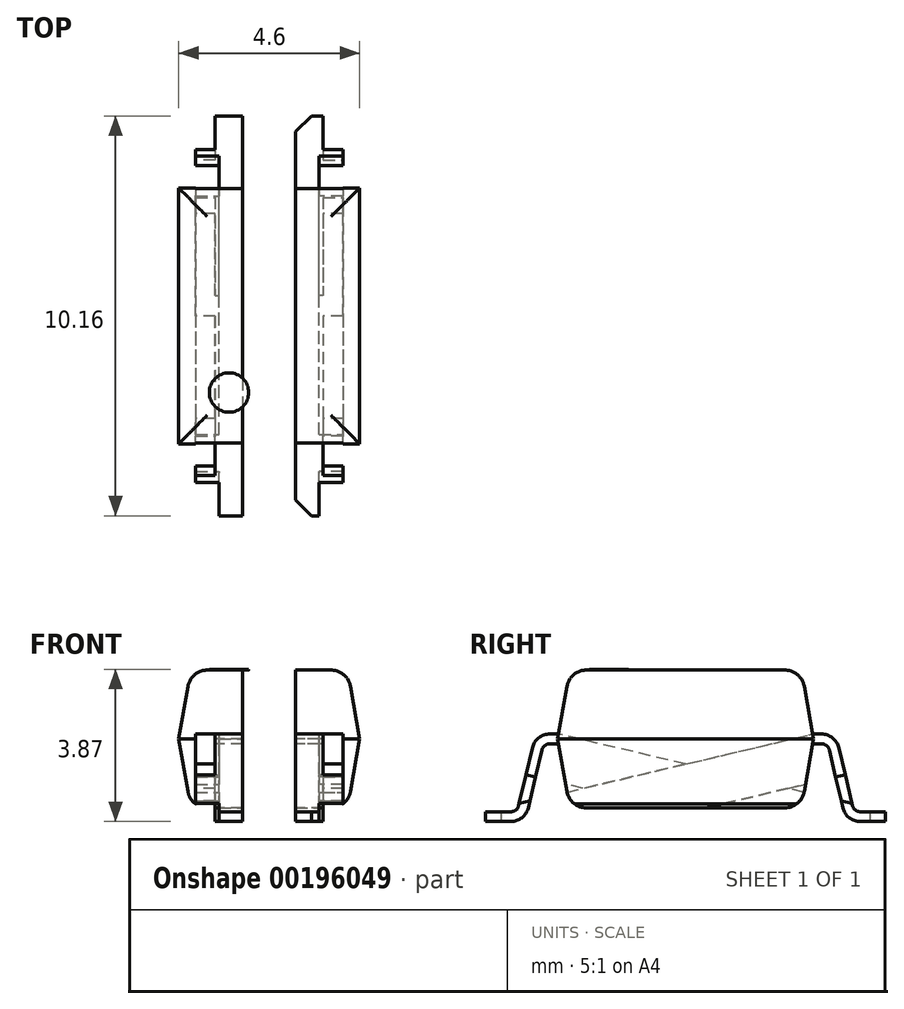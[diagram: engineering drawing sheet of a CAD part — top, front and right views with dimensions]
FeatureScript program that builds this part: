
annotation { "Feature Type Name" : "Feature", "Feature Type Description" : "" }
export const myFeature = defineFeature(function(context is Context, id is Id, definition is map)
    precondition{}
    {
        {
            var Q0;
            Q0=qCreatedBy(makeId("Top.planeOp"),FACE);
            var sketch = newSketch(context, id + "F0", { "sketchPlane" : qUnion([Q0])});
            skLineSegment(sketch, "E0.bottom", {"start": v(2.3, -3.25) * mm, "end": v(-2.3, -3.25) * mm});
            skLineSegment(sketch, "E0.top", {"start": v(2.3, 3.25) * mm, "end": v(-2.3, 3.25) * mm});
            skLineSegment(sketch, "E0.left", {"start": v(2.3, -3.25) * mm, "end": v(2.3, 3.25) * mm});
            skLineSegment(sketch, "E0.right", {"start": v(-2.3, -3.25) * mm, "end": v(-2.3, 3.25) * mm});
            skPoint(sketch, "E0.middle", {"position": v(0, 0) * mm});
            skSolve(sketch);
        }
        {
            var Q0;
            Q0 = qSketchRegion(id + "F0", true);
            extrude(context, id + "F1", {"entities" : qUnion([Q0]), "depth" : 1.75 * mm, "hasDraft" : true, "draftAngle" : 10 * degree, "draftPullDirection" : true});
        }
        {
            var Q0;
            Q0 = qSketchRegion(id + "F0", true);
            extrude(context, id + "F2", {"entities" : qUnion([Q0]), "operationType" : NewBodyOperationType.ADD, "oppositeDirection" : true, "depth" : 1.75 * mm, "hasDraft" : true, "draftAngle" : 10 * degree, "draftPullDirection" : true});
        }
        {
            var Q0;
            Q0=makeQuery(id+"F1.opExtrude","CAP_FACE",FACE,{"disambiguationData":[OSD([sQuery(id+"F0.wireOp",EDGE,"E0.bottom"),sQuery(id+"F0.wireOp",EDGE,"E0.top"),sQuery(id+"F0.wireOp",EDGE,"E0.left"),sQuery(id+"F0.wireOp",EDGE,"E0.right")])],"isStart":false});
            var Q1;
            Q1=makeQuery(id+"F2.opExtrude","CAP_FACE",FACE,{"disambiguationData":[OSD([sQuery(id+"F0.wireOp",EDGE,"E0.bottom"),sQuery(id+"F0.wireOp",EDGE,"E0.top"),sQuery(id+"F0.wireOp",EDGE,"E0.left"),sQuery(id+"F0.wireOp",EDGE,"E0.right")])],"isStart":false});
            fillet(context, id + "F3", {"entities" : qUnion([Q0, Q1]), "radius" : 0.5 * mm, "tangentPropagation" : true, "allowEdgeOverflow" : false});
        }
        {
            var Q0;
            Q0=qCreatedBy(makeId("Right.planeOp"),FACE);
            var sketch = newSketch(context, id + "F4", { "sketchPlane" : qUnion([Q0])});
            skLineSegment(sketch, "E1", {"start": v(3.81, 0.13) * mm, "end": v(4.28, -1.85) * mm});
            skLineSegment(sketch, "E2", {"start": v(4.28, -1.85) * mm, "end": v(5.08, -1.85) * mm});
            skLineSegment(sketch, "E3.0", {"start": v(4.08, -2.1) * mm, "end": v(5.08, -2.1) * mm});
            skLineSegment(sketch, "E4", {"start": v(5.08, -1.85) * mm, "end": v(5.08, -2.1) * mm});
            skLineSegment(sketch, "E5", {"start": v(0, 0) * mm, "end": v(0, -1.75) * mm, "construction": true});
            skLineSegment(sketch, "E6.MirrorCS", {"start": v(3.23, 0.13) * mm, "end": v(3.25, 0) * mm});
            skLineSegment(sketch, "E7", {"start": v(4.28, -1.85) * mm, "end": v(4.03, -1.9) * mm, "construction": true});
            skLineSegment(sketch, "E8", {"start": v(4.28, -1.85) * mm, "end": v(4.28, -2.1) * mm, "construction": true});
            skLineSegment(sketch, "E9", {"start": v(3.23, 0.13) * mm, "end": v(3.8, 0.13) * mm});
            skLineSegment(sketch, "E10", {"start": v(3.25, 0) * mm, "end": v(3.23, -0.12) * mm});
            skLineSegment(sketch, "E11", {"start": v(3.23, -0.12) * mm, "end": v(3.61, -0.12) * mm});
            skLineSegment(sketch, "E12", {"start": v(3.61, -0.12) * mm, "end": v(4.08, -2.1) * mm});
            skLineSegment(sketch, "E13", {"start": v(3.61, -0.12) * mm, "end": v(3.61, 0.13) * mm, "construction": true});
            skLineSegment(sketch, "E14.MirrorCS", {"start": v(-3.23, 0.13) * mm, "end": v(-3.25, 0) * mm});
            skLineSegment(sketch, "E15.MirrorCS", {"start": v(-3.25, 0) * mm, "end": v(-3.23, -0.12) * mm});
            skLineSegment(sketch, "E16.MirrorCS", {"start": v(-4.28, -1.85) * mm, "end": v(-4.03, -1.9) * mm, "construction": true});
            skLineSegment(sketch, "E17.MirrorCS", {"start": v(-5.08, -1.85) * mm, "end": v(-5.08, -2.1) * mm});
            skLineSegment(sketch, "E18.MirrorCS", {"start": v(-3.23, -0.12) * mm, "end": v(-3.61, -0.12) * mm});
            skLineSegment(sketch, "E19.MirrorCS", {"start": v(-3.61, -0.12) * mm, "end": v(-4.08, -2.1) * mm});
            skLineSegment(sketch, "E20.MirrorCS", {"start": v(-4.28, -1.85) * mm, "end": v(-4.28, -2.1) * mm, "construction": true});
            skLineSegment(sketch, "E21.MirrorCS", {"start": v(-3.61, -0.12) * mm, "end": v(-3.61, 0.13) * mm, "construction": true});
            skLineSegment(sketch, "E22.MirrorCS", {"start": v(-3.8, 0.12) * mm, "end": v(-4.28, -1.85) * mm});
            skLineSegment(sketch, "E23.MirrorCS", {"start": v(-4.28, -1.85) * mm, "end": v(-5.08, -1.85) * mm});
            skLineSegment(sketch, "E24.MirrorCS", {"start": v(-3.23, 0.13) * mm, "end": v(-3.8, 0.13) * mm});
            skLineSegment(sketch, "E25.MirrorCS", {"start": v(-4.08, -2.1) * mm, "end": v(-5.08, -2.1) * mm});
            skLineSegment(sketch, "E26", {"start": v(3.25, 0) * mm, "end": v(3.61, 0) * mm, "construction": true});
            skSolve(sketch);
        }
        {
            var Q0;
            Q0 = qSketchRegion(id + "F4", true);
            extrude(context, id + "F5", {"entities" : qUnion([Q0]), "endBound" : BoundingType.SYMMETRIC, "depth" : 3.74 * mm});
        }
        {
            var Q0;
            Q0=qCreatedBy(makeId("Top.planeOp"),FACE);
            var sketch = newSketch(context, id + "F6", { "sketchPlane" : qUnion([Q0])});
            skLineSegment(sketch, "E27.bottom", {"start": v(-0.67, 5.08) * mm, "end": v(0.67, 5.08) * mm});
            skLineSegment(sketch, "E27.top", {"start": v(-0.67, -5.08) * mm, "end": v(0.67, -5.08) * mm});
            skLineSegment(sketch, "E27.left", {"start": v(-0.67, 5.08) * mm, "end": v(-0.67, -5.08) * mm});
            skLineSegment(sketch, "E27.right", {"start": v(0.67, 5.08) * mm, "end": v(0.67, -5.08) * mm});
            skPoint(sketch, "E27.middle", {"position": v(0, 0) * mm});
            skSolve(sketch);
        }
        {
            var Q0;
            Q0 = qSketchRegion(id + "F6", true);
            extrude(context, id + "F7", {"entities" : qUnion([Q0]), "operationType" : NewBodyOperationType.REMOVE, "endBound" : BoundingType.THROUGH_ALL, "oppositeDirection" : true, "depth" : 25 * mm, "hasSecondDirection" : true, "secondDirectionBound" : SecondDirectionBoundingType.THROUGH_ALL, "secondDirectionOppositeDirection" : false, "secondDirectionDepth" : 25 * mm});
        }
        {
            var Q0;
            Q0=makeQuery(id+"F7.boolean.opBoolean","COPY",EDGE,{"derivedFrom":makeQuery(id+"F7.opExtrude","SWEPT_EDGE",EDGE,{"disambiguationData":[OSD([sQuery(id+"F6.wireOp",EDGE,"E27.top"),sQuery(id+"F6.wireOp",EDGE,"E27.left")])]})});
            var Q1;
            Q1=makeQuery(id+"F5.opExtrude","CAP_EDGE",EDGE,{"disambiguationData":[OSD([sQuery(id+"F4.wireOp",EDGE,"E17.MirrorCS")])],"isStart":true});
            var Q2;
            Q2=makeQuery(id+"F7.boolean.opBoolean","COPY",EDGE,{"derivedFrom":makeQuery(id+"F7.opExtrude","SWEPT_EDGE",EDGE,{"disambiguationData":[OSD([sQuery(id+"F6.wireOp",EDGE,"E27.top"),sQuery(id+"F6.wireOp",EDGE,"E27.right")])]})});
            var Q3;
            Q3=makeQuery(id+"F5.opExtrude","CAP_EDGE",EDGE,{"disambiguationData":[OSD([sQuery(id+"F4.wireOp",EDGE,"E17.MirrorCS")])],"isStart":false});
            var Q4;
            Q4=makeQuery(id+"F7.boolean.opBoolean","COPY",EDGE,{"derivedFrom":makeQuery(id+"F7.opExtrude","SWEPT_EDGE",EDGE,{"disambiguationData":[OSD([sQuery(id+"F6.wireOp",EDGE,"E27.bottom"),sQuery(id+"F6.wireOp",EDGE,"E27.right")])]})});
            var Q5;
            Q5=makeQuery(id+"F7.boolean.opBoolean","COPY",EDGE,{"derivedFrom":makeQuery(id+"F7.opExtrude","SWEPT_EDGE",EDGE,{"disambiguationData":[OSD([sQuery(id+"F6.wireOp",EDGE,"E27.bottom"),sQuery(id+"F6.wireOp",EDGE,"E27.left")])]})});
            var Q6;
            Q6=makeQuery(id+"F5.opExtrude","CAP_EDGE",EDGE,{"disambiguationData":[OSD([sQuery(id+"F4.wireOp",EDGE,"E4")])],"isStart":true});
            var Q7;
            Q7=makeQuery(id+"F5.opExtrude","CAP_EDGE",EDGE,{"disambiguationData":[OSD([sQuery(id+"F4.wireOp",EDGE,"E4")])],"isStart":false});
            chamfer(context, id + "F8", {"entities" : qUnion([Q0, Q1, Q2, Q3, Q4, Q5, Q6, Q7]), "width" : 0.4 * mm, "tangentPropagation" : true});
        }
        {
            var Q0;
            {var subQ2=sQuery(id+"F4.wireOp",EDGE,"E22.MirrorCS");Q0=makeQuery(id+"F7.boolean.opBoolean","SPLIT",FACE,{"disambiguationData":[TD([makeQuery(id+"F7.opExtrude","SWEPT_FACE",FACE,{"disambiguationData":[OSD([sQuery(id+"F6.wireOp",EDGE,"E27.left")])]})])],"derivedFrom":makeQuery(id+"F5.opExtrude","SWEPT_FACE",FACE,{"disambiguationData":[OSD([subQ2])]})});}
            var sketch = newSketch(context, id + "F9", { "sketchPlane" : qUnion([Q0])});
            skLineSegment(sketch, "E28.bottom", {"start": v(-1.87, -0.62) * mm, "end": v(-1.37, -0.62) * mm});
            skLineSegment(sketch, "E28.top", {"start": v(-1.87, -1.82) * mm, "end": v(-1.37, -1.82) * mm});
            skLineSegment(sketch, "E28.left", {"start": v(-1.87, -0.62) * mm, "end": v(-1.87, -1.82) * mm});
            skLineSegment(sketch, "E28.right", {"start": v(-1.37, -0.62) * mm, "end": v(-1.37, -1.82) * mm});
            skLineSegment(sketch, "E29", {"start": v(0, 0) * mm, "end": v(0, -3.26) * mm, "construction": true});
            skLineSegment(sketch, "E30.MirrorCS", {"start": v(1.87, -1.82) * mm, "end": v(1.37, -1.82) * mm});
            skLineSegment(sketch, "E31.MirrorCS", {"start": v(1.87, -0.62) * mm, "end": v(1.37, -0.62) * mm});
            skLineSegment(sketch, "E32.MirrorCS", {"start": v(1.37, -0.62) * mm, "end": v(1.37, -1.82) * mm});
            skLineSegment(sketch, "E33.MirrorCS", {"start": v(1.87, -0.62) * mm, "end": v(1.87, -1.82) * mm});
            skSolve(sketch);
        }
        {
            var Q0;
            Q0 = qSketchRegion(id + "F9", true);
            extrude(context, id + "F10", {"entities" : qUnion([Q0]), "operationType" : NewBodyOperationType.REMOVE, "oppositeDirection" : true, "depth" : 25 * mm});
        }
        {
            var Q0;
            {var subQ2=sQuery(id+"F4.wireOp",EDGE,"E1");Q0=makeQuery(id+"F7.boolean.opBoolean","SPLIT",FACE,{"disambiguationData":[TD([makeQuery(id+"F7.opExtrude","SWEPT_FACE",FACE,{"disambiguationData":[OSD([sQuery(id+"F6.wireOp",EDGE,"E27.right")])]})])],"derivedFrom":makeQuery(id+"F5.opExtrude","SWEPT_FACE",FACE,{"disambiguationData":[OSD([subQ2])]})});}
            var sketch = newSketch(context, id + "F11", { "sketchPlane" : qUnion([Q0])});
            skLineSegment(sketch, "E34.bottom", {"start": v(-1.87, -0.62) * mm, "end": v(-1.27, -0.62) * mm});
            skLineSegment(sketch, "E34.top", {"start": v(-1.87, -1.82) * mm, "end": v(-1.27, -1.82) * mm});
            skLineSegment(sketch, "E34.left", {"start": v(-1.87, -0.62) * mm, "end": v(-1.87, -1.82) * mm});
            skLineSegment(sketch, "E34.right", {"start": v(-1.27, -0.62) * mm, "end": v(-1.27, -1.82) * mm});
            skLineSegment(sketch, "E35", {"start": v(0, 0) * mm, "end": v(0, -3.04) * mm, "construction": true});
            skLineSegment(sketch, "E36.MirrorCS", {"start": v(1.87, -0.62) * mm, "end": v(1.27, -0.62) * mm});
            skLineSegment(sketch, "E37.MirrorCS", {"start": v(1.87, -1.82) * mm, "end": v(1.27, -1.82) * mm});
            skLineSegment(sketch, "E38.MirrorCS", {"start": v(1.87, -0.62) * mm, "end": v(1.87, -1.82) * mm});
            skLineSegment(sketch, "E39.MirrorCS", {"start": v(1.27, -0.62) * mm, "end": v(1.27, -1.82) * mm});
            skSolve(sketch);
        }
        {
            var Q0;
            Q0 = qSketchRegion(id + "F11", true);
            extrude(context, id + "F12", {"entities" : qUnion([Q0]), "operationType" : NewBodyOperationType.REMOVE, "oppositeDirection" : true, "depth" : 25 * mm});
        }
        {
            var Q0;
            Q0=makeQuery(id+"F1.opExtrude","CAP_FACE",FACE,{"disambiguationData":[OSD([sQuery(id+"F0.wireOp",EDGE,"E0.bottom"),sQuery(id+"F0.wireOp",EDGE,"E0.top"),sQuery(id+"F0.wireOp",EDGE,"E0.left"),sQuery(id+"F0.wireOp",EDGE,"E0.right")])],"isStart":false});
            var sketch = newSketch(context, id + "F13", { "sketchPlane" : qUnion([Q0])});
            skCircle(sketch, "E40", {"center": v(-1.02, -1.95) * mm, "radius": 0.5 * mm});
            skLineSegment(sketch, "E41", {"start": v(-1.02, -3.23) * mm, "end": v(-1.02, -1.95) * mm, "construction": true});
            skLineSegment(sketch, "E42", {"start": v(-1.02, -1.95) * mm, "end": v(-2.3, -1.95) * mm, "construction": true});
            skSolve(sketch);
        }
        {
            var Q0;
            Q0 = qSketchRegion(id + "F13", true);
            extrude(context, id + "F14", {"entities" : qUnion([Q0]), "depth" : 0.02 * mm});
        }
        {
            var Q0;
            {var subQ0=sQuery(id+"F4.wireOp",EDGE,"E23.MirrorCS");var subQ1=sQuery(id+"F4.wireOp",EDGE,"E22.MirrorCS");Q0=makeQuery(id+"F7.boolean.opBoolean","SPLIT",EDGE,{"disambiguationData":[TD([makeQuery(id+"F7.opExtrude","SWEPT_FACE",FACE,{"disambiguationData":[OSD([sQuery(id+"F6.wireOp",EDGE,"E27.left")])]})])],"derivedFrom":makeQuery(id+"F5.opExtrude","SWEPT_EDGE",EDGE,{"disambiguationData":[OSD([subQ1,subQ0])]})});}
            var Q1;
            {var subQ0=sQuery(id+"F4.wireOp",EDGE,"E23.MirrorCS");var subQ1=sQuery(id+"F4.wireOp",EDGE,"E22.MirrorCS");Q1=makeQuery(id+"F7.boolean.opBoolean","SPLIT",EDGE,{"disambiguationData":[TD([makeQuery(id+"F7.opExtrude","SWEPT_FACE",FACE,{"disambiguationData":[OSD([sQuery(id+"F6.wireOp",EDGE,"E27.right")])]})])],"derivedFrom":makeQuery(id+"F5.opExtrude","SWEPT_EDGE",EDGE,{"disambiguationData":[OSD([subQ1,subQ0])]})});}
            var Q2;
            {var subQ0=sQuery(id+"F4.wireOp",EDGE,"E19.MirrorCS");var subQ1=sQuery(id+"F4.wireOp",EDGE,"E18.MirrorCS");Q2=makeQuery(id+"F7.boolean.opBoolean","SPLIT",EDGE,{"disambiguationData":[TD([makeQuery(id+"F7.opExtrude","SWEPT_FACE",FACE,{"disambiguationData":[OSD([sQuery(id+"F6.wireOp",EDGE,"E27.right")])]})])],"derivedFrom":makeQuery(id+"F5.opExtrude","SWEPT_EDGE",EDGE,{"disambiguationData":[OSD([subQ1,subQ0])]})});}
            var Q3;
            {var subQ0=sQuery(id+"F4.wireOp",EDGE,"E19.MirrorCS");var subQ1=sQuery(id+"F4.wireOp",EDGE,"E18.MirrorCS");Q3=makeQuery(id+"F7.boolean.opBoolean","SPLIT",EDGE,{"disambiguationData":[TD([makeQuery(id+"F7.opExtrude","SWEPT_FACE",FACE,{"disambiguationData":[OSD([sQuery(id+"F6.wireOp",EDGE,"E27.left")])]})])],"derivedFrom":makeQuery(id+"F5.opExtrude","SWEPT_EDGE",EDGE,{"disambiguationData":[OSD([subQ1,subQ0])]})});}
            var Q4;
            {var subQ0=sQuery(id+"F4.wireOp",EDGE,"E12");var subQ1=sQuery(id+"F4.wireOp",EDGE,"E11");Q4=makeQuery(id+"F7.boolean.opBoolean","SPLIT",EDGE,{"disambiguationData":[TD([makeQuery(id+"F7.opExtrude","SWEPT_FACE",FACE,{"disambiguationData":[OSD([sQuery(id+"F6.wireOp",EDGE,"E27.right")])]})])],"derivedFrom":makeQuery(id+"F5.opExtrude","SWEPT_EDGE",EDGE,{"disambiguationData":[OSD([subQ1,subQ0])]})});}
            var Q5;
            {var subQ0=sQuery(id+"F4.wireOp",EDGE,"E12");var subQ1=sQuery(id+"F4.wireOp",EDGE,"E11");Q5=makeQuery(id+"F7.boolean.opBoolean","SPLIT",EDGE,{"disambiguationData":[TD([makeQuery(id+"F7.opExtrude","SWEPT_FACE",FACE,{"disambiguationData":[OSD([sQuery(id+"F6.wireOp",EDGE,"E27.left")])]})])],"derivedFrom":makeQuery(id+"F5.opExtrude","SWEPT_EDGE",EDGE,{"disambiguationData":[OSD([subQ1,subQ0])]})});}
            var Q6;
            {var subQ0=sQuery(id+"F4.wireOp",EDGE,"E1");var subQ1=sQuery(id+"F4.wireOp",EDGE,"E2");Q6=makeQuery(id+"F7.boolean.opBoolean","SPLIT",EDGE,{"disambiguationData":[TD([makeQuery(id+"F7.opExtrude","SWEPT_FACE",FACE,{"disambiguationData":[OSD([sQuery(id+"F6.wireOp",EDGE,"E27.right")])]})])],"derivedFrom":makeQuery(id+"F5.opExtrude","SWEPT_EDGE",EDGE,{"disambiguationData":[OSD([subQ0,subQ1])]})});}
            var Q7;
            {var subQ0=sQuery(id+"F4.wireOp",EDGE,"E1");var subQ1=sQuery(id+"F4.wireOp",EDGE,"E2");Q7=makeQuery(id+"F7.boolean.opBoolean","SPLIT",EDGE,{"disambiguationData":[TD([makeQuery(id+"F7.opExtrude","SWEPT_FACE",FACE,{"disambiguationData":[OSD([sQuery(id+"F6.wireOp",EDGE,"E27.left")])]})])],"derivedFrom":makeQuery(id+"F5.opExtrude","SWEPT_EDGE",EDGE,{"disambiguationData":[OSD([subQ0,subQ1])]})});}
            fillet(context, id + "F15", {"entities" : qUnion([Q0, Q1, Q2, Q3, Q4, Q5, Q6, Q7]), "radius" : 0.2 * mm, "tangentPropagation" : true, "allowEdgeOverflow" : false});
        }
        {
            var Q0;
            {var subQ0=sQuery(id+"F4.wireOp",EDGE,"E1");var subQ1=sQuery(id+"F4.wireOp",EDGE,"E9");Q0=makeQuery(id+"F7.boolean.opBoolean","SPLIT",EDGE,{"disambiguationData":[TD([makeQuery(id+"F7.opExtrude","SWEPT_FACE",FACE,{"disambiguationData":[OSD([sQuery(id+"F6.wireOp",EDGE,"E27.right")])]})])],"derivedFrom":makeQuery(id+"F5.opExtrude","SWEPT_EDGE",EDGE,{"disambiguationData":[OSD([subQ0,subQ1])]})});}
            var Q1;
            {var subQ0=sQuery(id+"F4.wireOp",EDGE,"E1");var subQ1=sQuery(id+"F4.wireOp",EDGE,"E9");Q1=makeQuery(id+"F7.boolean.opBoolean","SPLIT",EDGE,{"disambiguationData":[TD([makeQuery(id+"F7.opExtrude","SWEPT_FACE",FACE,{"disambiguationData":[OSD([sQuery(id+"F6.wireOp",EDGE,"E27.left")])]})])],"derivedFrom":makeQuery(id+"F5.opExtrude","SWEPT_EDGE",EDGE,{"disambiguationData":[OSD([subQ0,subQ1])]})});}
            var Q2;
            {var subQ0=sQuery(id+"F4.wireOp",EDGE,"E12");var subQ1=sQuery(id+"F4.wireOp",EDGE,"E3.0");Q2=makeQuery(id+"F7.boolean.opBoolean","SPLIT",EDGE,{"disambiguationData":[TD([makeQuery(id+"F7.opExtrude","SWEPT_FACE",FACE,{"disambiguationData":[OSD([sQuery(id+"F6.wireOp",EDGE,"E27.right")])]})])],"derivedFrom":makeQuery(id+"F5.opExtrude","SWEPT_EDGE",EDGE,{"disambiguationData":[OSD([subQ1,subQ0])]})});}
            var Q3;
            {var subQ0=sQuery(id+"F4.wireOp",EDGE,"E12");var subQ1=sQuery(id+"F4.wireOp",EDGE,"E3.0");Q3=makeQuery(id+"F7.boolean.opBoolean","SPLIT",EDGE,{"disambiguationData":[TD([makeQuery(id+"F7.opExtrude","SWEPT_FACE",FACE,{"disambiguationData":[OSD([sQuery(id+"F6.wireOp",EDGE,"E27.left")])]})])],"derivedFrom":makeQuery(id+"F5.opExtrude","SWEPT_EDGE",EDGE,{"disambiguationData":[OSD([subQ1,subQ0])]})});}
            var Q4;
            {var subQ0=sQuery(id+"F4.wireOp",EDGE,"E24.MirrorCS");var subQ1=sQuery(id+"F4.wireOp",EDGE,"E22.MirrorCS");Q4=makeQuery(id+"F7.boolean.opBoolean","SPLIT",EDGE,{"disambiguationData":[TD([makeQuery(id+"F7.opExtrude","SWEPT_FACE",FACE,{"disambiguationData":[OSD([sQuery(id+"F6.wireOp",EDGE,"E27.right")])]})])],"derivedFrom":makeQuery(id+"F5.opExtrude","SWEPT_EDGE",EDGE,{"disambiguationData":[OSD([subQ1,subQ0])]})});}
            var Q5;
            {var subQ0=sQuery(id+"F4.wireOp",EDGE,"E24.MirrorCS");var subQ1=sQuery(id+"F4.wireOp",EDGE,"E22.MirrorCS");Q5=makeQuery(id+"F7.boolean.opBoolean","SPLIT",EDGE,{"disambiguationData":[TD([makeQuery(id+"F7.opExtrude","SWEPT_FACE",FACE,{"disambiguationData":[OSD([sQuery(id+"F6.wireOp",EDGE,"E27.left")])]})])],"derivedFrom":makeQuery(id+"F5.opExtrude","SWEPT_EDGE",EDGE,{"disambiguationData":[OSD([subQ1,subQ0])]})});}
            var Q6;
            {var subQ0=sQuery(id+"F4.wireOp",EDGE,"E25.MirrorCS");var subQ1=sQuery(id+"F4.wireOp",EDGE,"E19.MirrorCS");Q6=makeQuery(id+"F7.boolean.opBoolean","SPLIT",EDGE,{"disambiguationData":[TD([makeQuery(id+"F7.opExtrude","SWEPT_FACE",FACE,{"disambiguationData":[OSD([sQuery(id+"F6.wireOp",EDGE,"E27.right")])]})])],"derivedFrom":makeQuery(id+"F5.opExtrude","SWEPT_EDGE",EDGE,{"disambiguationData":[OSD([subQ1,subQ0])]})});}
            var Q7;
            {var subQ0=sQuery(id+"F4.wireOp",EDGE,"E25.MirrorCS");var subQ1=sQuery(id+"F4.wireOp",EDGE,"E19.MirrorCS");Q7=makeQuery(id+"F7.boolean.opBoolean","SPLIT",EDGE,{"disambiguationData":[TD([makeQuery(id+"F7.opExtrude","SWEPT_FACE",FACE,{"disambiguationData":[OSD([sQuery(id+"F6.wireOp",EDGE,"E27.left")])]})])],"derivedFrom":makeQuery(id+"F5.opExtrude","SWEPT_EDGE",EDGE,{"disambiguationData":[OSD([subQ1,subQ0])]})});}
            fillet(context, id + "F16", {"entities" : qUnion([Q0, Q1, Q2, Q3, Q4, Q5, Q6, Q7]), "radius" : 0.46 * mm, "tangentPropagation" : true, "allowEdgeOverflow" : false});
        }
    });
